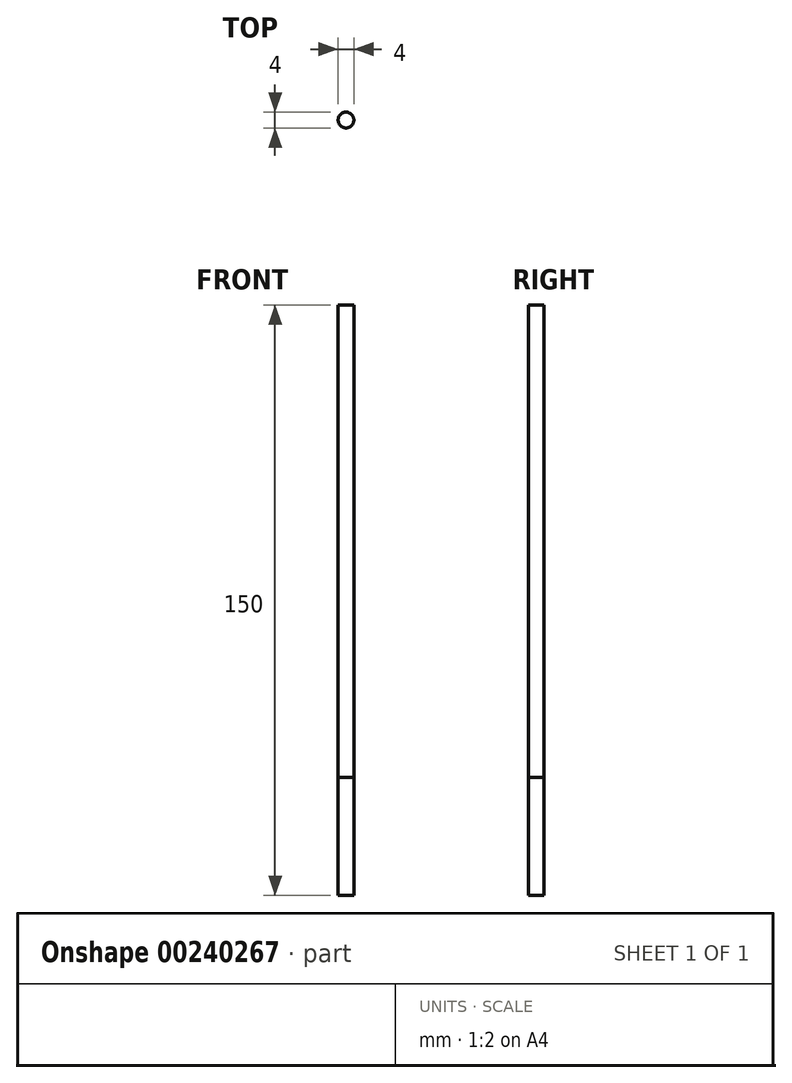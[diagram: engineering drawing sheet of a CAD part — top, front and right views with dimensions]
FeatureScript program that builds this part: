
annotation { "Feature Type Name" : "Feature", "Feature Type Description" : "" }
export const myFeature = defineFeature(function(context is Context, id is Id, definition is map)
    precondition{}
    {
        {
            var Q0;
            Q0=qCreatedBy(makeId("Top.planeOp"),FACE);
            var sketch = newSketch(context, id + "F0", { "sketchPlane" : qUnion([Q0])});
            skCircle(sketch, "E0", {"center": v(0, 0) * mm, "radius": 2 * mm});
            skSolve(sketch);
        }
        {
            var Q0;
            Q0 = qSketchRegion(id + "F0", true);
            extrude(context, id + "F1", {"entities" : qUnion([Q0]), "depth" : 150 * mm});
        }
        {
            var Q0;
            Q0 = qSketchRegion(id + "F0", true);
            extrude(context, id + "F2", {"entities" : qUnion([Q0]), "depth" : 30 * mm});
        }
    });
